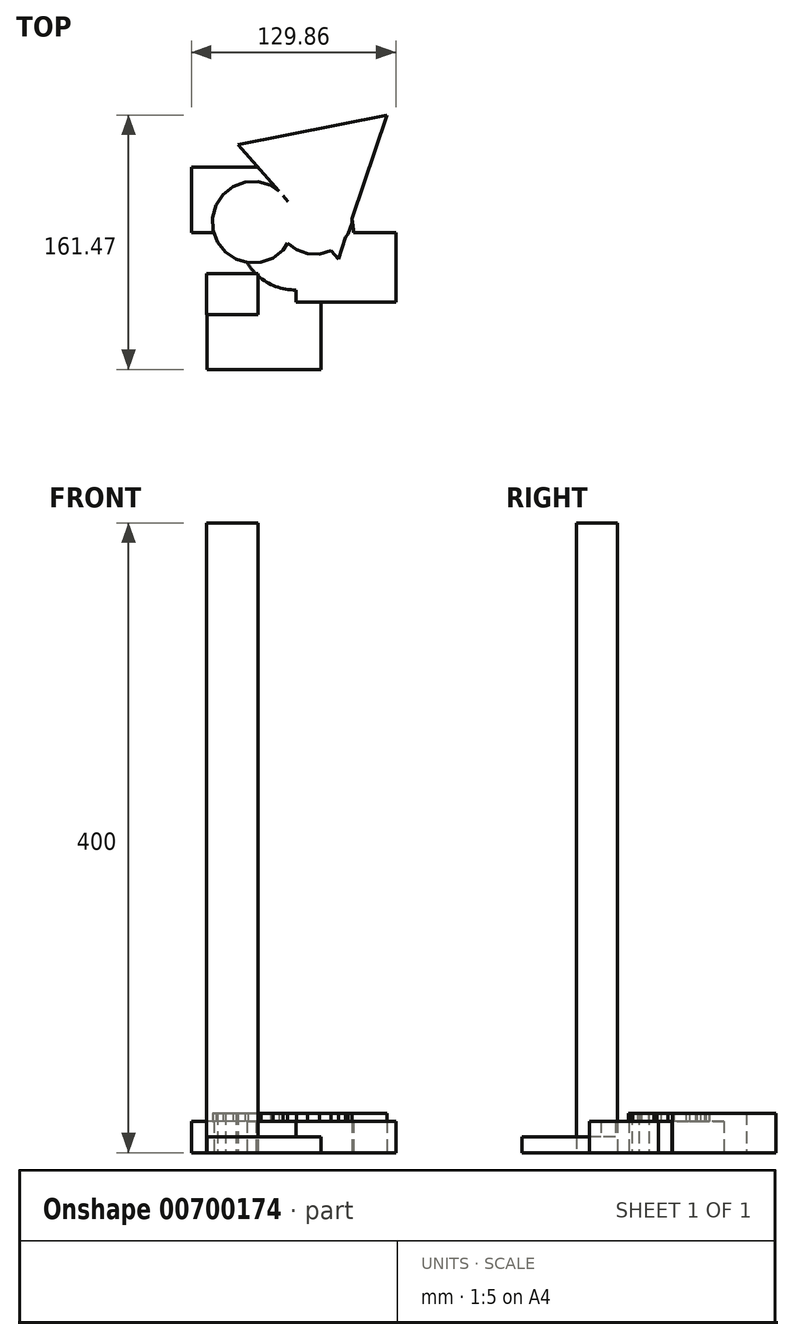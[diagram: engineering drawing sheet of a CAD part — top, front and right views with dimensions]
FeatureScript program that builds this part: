
annotation { "Feature Type Name" : "Feature", "Feature Type Description" : "" }
export const myFeature = defineFeature(function(context is Context, id is Id, definition is map)
    precondition{}
    {
        {
            var Q0;
            Q0=qCreatedBy(makeId("Top.planeOp"),FACE);
            var sketch = newSketch(context, id + "F0", { "sketchPlane" : qUnion([Q0])});
            skLineSegment(sketch, "E0.bottom", {"start": v(0, 0) * mm, "end": v(-66.44, 0) * mm});
            skLineSegment(sketch, "E0.top", {"start": v(0, 41.49) * mm, "end": v(-66.44, 41.49) * mm});
            skLineSegment(sketch, "E0.left", {"start": v(0, 0) * mm, "end": v(0, 41.49) * mm});
            skLineSegment(sketch, "E0.right", {"start": v(-66.44, 0) * mm, "end": v(-66.44, 41.49) * mm});
            skLineSegment(sketch, "E1.bottom", {"start": v(0, 0) * mm, "end": v(63.42, 0) * mm});
            skLineSegment(sketch, "E1.top", {"start": v(0, -44.05) * mm, "end": v(63.42, -44.05) * mm});
            skLineSegment(sketch, "E1.left", {"start": v(0, 0) * mm, "end": v(0, -44.05) * mm});
            skLineSegment(sketch, "E1.right", {"start": v(63.42, 0) * mm, "end": v(63.42, -44.05) * mm});
            skCircle(sketch, "E2", {"center": v(0, 0) * mm, "radius": 36.5 * mm});
            skSolve(sketch);
        }
        {
            var Q0;
            Q0 = qSketchRegion(id + "F0", true);
            extrude(context, id + "F1", {"entities" : qUnion([Q0]), "depth" : 20 * mm, "offsetDistance" : 25 * mm});
        }
        {
            var Q0;
            Q0=qCreatedBy(makeId("Top.planeOp"),FACE);
            var sketch = newSketch(context, id + "F2", { "sketchPlane" : qUnion([Q0])});
            skCircle(sketch, "E3.cCircle", {"center": v(16.01, 37.89) * mm, "radius": 27.83 * mm, "construction": true});
            skLineSegment(sketch, "E3.0", {"start": v(-36.7, 55.8) * mm, "end": v(57.87, 74.58) * mm});
            skLineSegment(sketch, "E3.1", {"start": v(57.87, 74.58) * mm, "end": v(26.86, -16.71) * mm});
            skLineSegment(sketch, "E3.2", {"start": v(26.86, -16.71) * mm, "end": v(-36.7, 55.8) * mm});
            skPoint(sketch, "E3.0.midPoint", {"position": v(10.59, 65.19) * mm});
            skCircle(sketch, "E4.cCircle", {"center": v(11.72, 10.39) * mm, "radius": 23.83 * mm, "construction": true});
            skLineSegment(sketch, "E4.0", {"start": v(-12.01, 14.73) * mm, "end": v(-9.51, 21.85) * mm});
            skLineSegment(sketch, "E4.1", {"start": v(-9.51, 21.85) * mm, "end": v(-4.93, 27.85) * mm});
            skLineSegment(sketch, "E4.2", {"start": v(-4.93, 27.85) * mm, "end": v(1.28, 32.14) * mm});
            skLineSegment(sketch, "E4.3", {"start": v(1.28, 32.14) * mm, "end": v(8.51, 34.3) * mm});
            skLineSegment(sketch, "E4.4", {"start": v(8.51, 34.3) * mm, "end": v(16.06, 34.12) * mm});
            skLineSegment(sketch, "E4.5", {"start": v(16.06, 34.12) * mm, "end": v(23.18, 31.62) * mm});
            skLineSegment(sketch, "E4.6", {"start": v(23.18, 31.62) * mm, "end": v(29.18, 27.03) * mm});
            skLineSegment(sketch, "E4.7", {"start": v(29.18, 27.03) * mm, "end": v(33.47, 20.82) * mm});
            skLineSegment(sketch, "E4.8", {"start": v(33.47, 20.82) * mm, "end": v(35.63, 13.6) * mm});
            skLineSegment(sketch, "E4.9", {"start": v(35.63, 13.6) * mm, "end": v(35.45, 6.05) * mm});
            skLineSegment(sketch, "E4.10", {"start": v(35.45, 6.05) * mm, "end": v(32.94, -1.07) * mm});
            skLineSegment(sketch, "E4.11", {"start": v(32.94, -1.07) * mm, "end": v(28.36, -7.07) * mm});
            skLineSegment(sketch, "E4.12", {"start": v(28.36, -7.07) * mm, "end": v(22.15, -11.36) * mm});
            skLineSegment(sketch, "E4.13", {"start": v(22.15, -11.36) * mm, "end": v(14.92, -13.52) * mm});
            skLineSegment(sketch, "E4.14", {"start": v(14.92, -13.52) * mm, "end": v(7.38, -13.34) * mm});
            skLineSegment(sketch, "E4.15", {"start": v(7.38, -13.34) * mm, "end": v(0.26, -10.84) * mm});
            skLineSegment(sketch, "E4.16", {"start": v(0.26, -10.84) * mm, "end": v(-5.74, -6.26) * mm});
            skLineSegment(sketch, "E4.17", {"start": v(-5.74, -6.26) * mm, "end": v(-10.03, -0.05) * mm});
            skLineSegment(sketch, "E4.18", {"start": v(-10.03, -0.05) * mm, "end": v(-12.2, 7.18) * mm});
            skLineSegment(sketch, "E4.19", {"start": v(-12.2, 7.18) * mm, "end": v(-12.01, 14.73) * mm});
            skPoint(sketch, "E4.0.midPoint", {"position": v(-10.76, 18.29) * mm});
            skCircle(sketch, "E5.cCircle", {"center": v(-27.24, 6.55) * mm, "radius": 25.58 * mm, "construction": true});
            skLineSegment(sketch, "E5.0", {"start": v(-16.32, 30.03) * mm, "end": v(-9.6, 25.5) * mm});
            skLineSegment(sketch, "E5.1", {"start": v(-9.6, 25.5) * mm, "end": v(-4.6, 19.13) * mm});
            skLineSegment(sketch, "E5.2", {"start": v(-4.6, 19.13) * mm, "end": v(-1.82, 11.52) * mm});
            skLineSegment(sketch, "E5.3", {"start": v(-1.82, 11.52) * mm, "end": v(-1.53, 3.42) * mm});
            skLineSegment(sketch, "E5.4", {"start": v(-1.53, 3.42) * mm, "end": v(-3.75, -4.37) * mm});
            skLineSegment(sketch, "E5.5", {"start": v(-3.75, -4.37) * mm, "end": v(-8.28, -11.09) * mm});
            skLineSegment(sketch, "E5.6", {"start": v(-8.28, -11.09) * mm, "end": v(-14.66, -16.08) * mm});
            skLineSegment(sketch, "E5.7", {"start": v(-14.66, -16.08) * mm, "end": v(-22.27, -18.86) * mm});
            skLineSegment(sketch, "E5.8", {"start": v(-22.27, -18.86) * mm, "end": v(-30.36, -19.16) * mm});
            skLineSegment(sketch, "E5.9", {"start": v(-30.36, -19.16) * mm, "end": v(-38.15, -16.93) * mm});
            skLineSegment(sketch, "E5.10", {"start": v(-38.15, -16.93) * mm, "end": v(-44.87, -12.41) * mm});
            skLineSegment(sketch, "E5.11", {"start": v(-44.87, -12.41) * mm, "end": v(-49.87, -6.03) * mm});
            skLineSegment(sketch, "E5.12", {"start": v(-49.87, -6.03) * mm, "end": v(-52.65, 1.58) * mm});
            skLineSegment(sketch, "E5.13", {"start": v(-52.65, 1.58) * mm, "end": v(-52.94, 9.67) * mm});
            skLineSegment(sketch, "E5.14", {"start": v(-52.94, 9.67) * mm, "end": v(-50.72, 17.46) * mm});
            skLineSegment(sketch, "E5.15", {"start": v(-50.72, 17.46) * mm, "end": v(-46.2, 24.19) * mm});
            skLineSegment(sketch, "E5.16", {"start": v(-46.2, 24.19) * mm, "end": v(-39.82, 29.18) * mm});
            skLineSegment(sketch, "E5.17", {"start": v(-39.82, 29.18) * mm, "end": v(-32.2, 31.96) * mm});
            skLineSegment(sketch, "E5.18", {"start": v(-32.2, 31.96) * mm, "end": v(-24.11, 32.25) * mm});
            skLineSegment(sketch, "E5.19", {"start": v(-24.11, 32.25) * mm, "end": v(-16.32, 30.03) * mm});
            skPoint(sketch, "E5.0.midPoint", {"position": v(-12.96, 27.77) * mm});
            skSolve(sketch);
        }
        {
            var Q0;
            Q0 = qSketchRegion(id + "F2", true);
            extrude(context, id + "F3", {"entities" : qUnion([Q0]), "operationType" : NewBodyOperationType.ADD, "depth" : 25 * mm, "offsetDistance" : 25 * mm});
        }
        {
            var Q0;
            Q0=qCreatedBy(makeId("Top.planeOp"),FACE);
            var sketch = newSketch(context, id + "F4", { "sketchPlane" : qUnion([Q0])});
            skLineSegment(sketch, "E6.bottom", {"start": v(-56.96, -26.16) * mm, "end": v(-24.06, -26.16) * mm});
            skLineSegment(sketch, "E6.top", {"start": v(-56.96, -52.06) * mm, "end": v(-24.06, -52.06) * mm});
            skLineSegment(sketch, "E6.left", {"start": v(-56.96, -26.16) * mm, "end": v(-56.96, -52.06) * mm});
            skLineSegment(sketch, "E6.right", {"start": v(-24.06, -26.16) * mm, "end": v(-24.06, -52.06) * mm});
            skSolve(sketch);
        }
        {
            var Q0;
            Q0 = qSketchRegion(id + "F4", true);
            extrude(context, id + "F5", {"entities" : qUnion([Q0]), "operationType" : NewBodyOperationType.ADD, "depth" : 400 * mm, "offsetDistance" : 25 * mm});
        }
        {
            var Q0;
            Q0=qCreatedBy(makeId("Top.planeOp"),FACE);
            var sketch = newSketch(context, id + "F6", { "sketchPlane" : qUnion([Q0])});
            skLineSegment(sketch, "E7.bottom", {"start": v(-56.48, -26.33) * mm, "end": v(15.8, -26.33) * mm});
            skLineSegment(sketch, "E7.top", {"start": v(-56.48, -86.89) * mm, "end": v(15.8, -86.89) * mm});
            skLineSegment(sketch, "E7.left", {"start": v(-56.48, -26.33) * mm, "end": v(-56.48, -86.89) * mm});
            skLineSegment(sketch, "E7.right", {"start": v(15.8, -26.33) * mm, "end": v(15.8, -86.89) * mm});
            skSolve(sketch);
        }
        {
            var Q0;
            Q0 = qSketchRegion(id + "F6", true);
            extrude(context, id + "F7", {"entities" : qUnion([Q0]), "operationType" : NewBodyOperationType.ADD, "depth" : 10 * mm, "offsetDistance" : 25 * mm});
        }
    });
